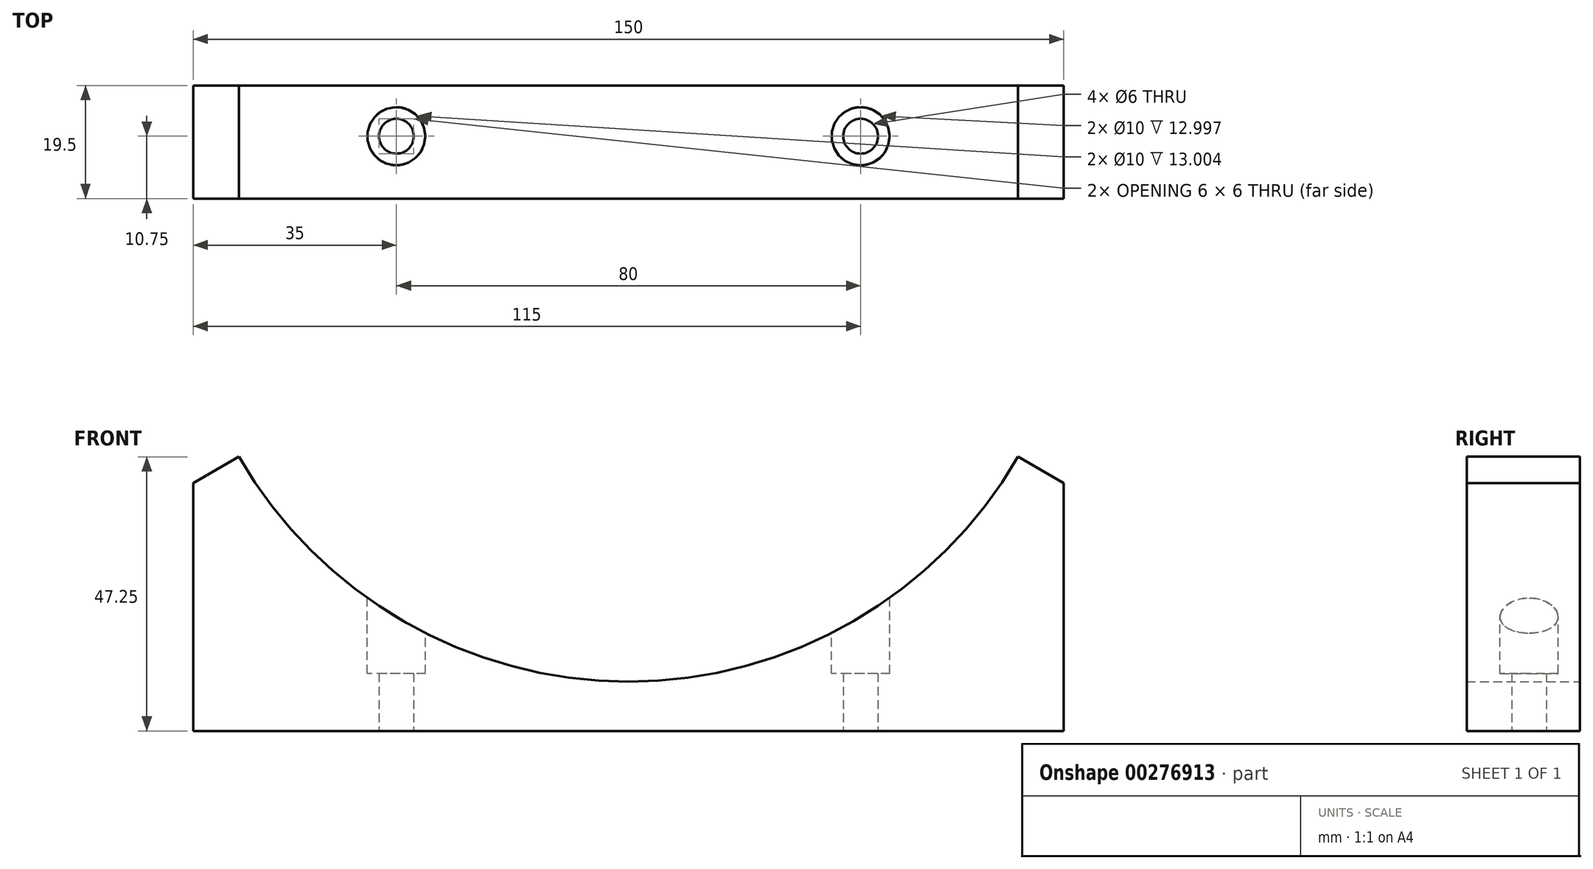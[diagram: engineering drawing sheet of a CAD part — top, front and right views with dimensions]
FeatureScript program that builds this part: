
annotation { "Feature Type Name" : "Feature", "Feature Type Description" : "" }
export const myFeature = defineFeature(function(context is Context, id is Id, definition is map)
    precondition{}
    {
        {
            var Q0;
            Q0=qCreatedBy(makeId("Front.planeOp"),FACE);
            var sketch = newSketch(context, id + "F0", { "sketchPlane" : qUnion([Q0])});
            skLineSegment(sketch, "E0.bottom", {"start": v(-75, -19.37) * mm, "end": v(75, -19.37) * mm});
            skLineSegment(sketch, "E0.left", {"start": v(-75, -19.37) * mm, "end": v(-75, 23.33) * mm});
            skLineSegment(sketch, "E0.right", {"start": v(75, -19.37) * mm, "end": v(75, 23.33) * mm});
            skLineSegment(sketch, "E1.trimOffspring", {"start": v(-67.12, 27.88) * mm, "end": v(-75, 23.33) * mm});
            skLineSegment(sketch, "E2.trimOffspring", {"start": v(67.12, 27.88) * mm, "end": v(75, 23.33) * mm});
            skLineSegment(sketch, "E3", {"start": v(0, 66.63) * mm, "end": v(0, -19.37) * mm, "construction": true});
            skPoint(sketch, "E3.endSnap0", {"position": v(0, -12) * mm});
            skLineSegment(sketch, "E4", {"start": v(0, 66.63) * mm, "end": v(75, 23.33) * mm, "construction": true});
            skArc(sketch, "E5", {"start": v(-67.12, 27.88) * mm, "mid": v(0, -10.87) * mm, "end": v(67.12, 27.88) * mm});
            skLineSegment(sketch, "E6", {"start": v(0, -19.37) * mm, "end": v(0, -10.87) * mm, "construction": true});
            skSolve(sketch);
        }
        {
            var Q0;
            Q0=qSketchRegion(id+"F0",true);
            extrude(context, id + "F1", {"entities" : qUnion([Q0]), "depth" : 19.5 * mm});
        }
        {
            var Q0;
            Q0=makeQuery(id+"F1.opExtrude","SWEPT_FACE",FACE,{"disambiguationData":[OSD([sQuery(id+"F0.wireOp",EDGE,"E0.bottom")])]});
            var sketch = newSketch(context, id + "F2", { "sketchPlane" : qUnion([Q0])});
            skCircle(sketch, "E7", {"center": v(40, 8.75) * mm, "radius": 3 * mm});
            skCircle(sketch, "E8", {"center": v(-40, 8.75) * mm, "radius": 3 * mm});
            skLineSegment(sketch, "E9", {"start": v(0, 0) * mm, "end": v(0, 19.5) * mm, "construction": true});
            skSolve(sketch);
        }
        {
            var Q0;
            Q0=makeQuery(id+"F2.imprint","IMPRINT",FACE,{"disambiguationData":[TD([[makeQuery(id+"F2.imprint","IMPRINT",EDGE,{"derivedFrom":sQuery(id+"F2.wireOp",EDGE,"E7")}),1.0]])]});
            var Q1;
            Q1=makeQuery(id+"F2.imprint","IMPRINT",FACE,{"disambiguationData":[TD([[makeQuery(id+"F2.imprint","IMPRINT",EDGE,{"derivedFrom":sQuery(id+"F2.wireOp",EDGE,"E8")}),1.0]])]});
            extrude(context, id + "F3", {"entities" : qUnion([Q0, Q1]), "operationType" : NewBodyOperationType.REMOVE, "endBound" : BoundingType.THROUGH_ALL, "oppositeDirection" : true, "depth" : 25 * mm});
        }
        {
            var Q0;
            Q0=qCreatedBy(makeId("Top.planeOp"),FACE);
            cPlane(context, id + "F4", {"entities" : qUnion([Q0]), "cplaneType" : CPlaneType.OFFSET, "offset" : 15 * mm, "width" : 150 * mm, "height" : 150 * mm});
        }
        {
            var Q0;
            Q0=qCreatedBy(id+"F4.planeOp",FACE);
            var sketch = newSketch(context, id + "F5", { "sketchPlane" : qUnion([Q0])});
            skCircle(sketch, "E10", {"center": v(-40, -8.75) * mm, "radius": 5 * mm});
            skCircle(sketch, "E11", {"center": v(40, -8.75) * mm, "radius": 5 * mm});
            skSolve(sketch);
        }
        {
            var Q0;
            Q0=makeQuery(id+"F5.imprint","IMPRINT",FACE,{"disambiguationData":[TD([[makeQuery(id+"F5.imprint","IMPRINT",EDGE,{"derivedFrom":sQuery(id+"F5.wireOp",EDGE,"E10")}),1.0]])]});
            var Q1;
            Q1=makeQuery(id+"F5.imprint","IMPRINT",FACE,{"disambiguationData":[TD([[makeQuery(id+"F5.imprint","IMPRINT",EDGE,{"derivedFrom":sQuery(id+"F5.wireOp",EDGE,"E11")}),1.0]])]});
            extrude(context, id + "F6", {"entities" : qUnion([Q0, Q1]), "operationType" : NewBodyOperationType.REMOVE, "oppositeDirection" : true, "depth" : 24.46 * mm});
        }
        {
            var Q0;
            Q0=qCreatedBy(makeId("Right.planeOp"),FACE);
            cPlane(context, id + "F7", {"entities" : qUnion([Q0]), "cplaneType" : CPlaneType.OFFSET, "offset" : 36 * mm, "width" : 150 * mm, "height" : 150 * mm});
        }
        {
            var Q0;
            Q0=makeQuery(id+"F1.opExtrude","SWEPT_BODY",BODY,{"disambiguationData":[OSD([sQuery(id+"F0.wireOp",EDGE,"E0.bottom"),sQuery(id+"F0.wireOp",EDGE,"E0.left"),sQuery(id+"F0.wireOp",EDGE,"E0.right"),sQuery(id+"F0.wireOp",EDGE,"E1.trimOffspring"),sQuery(id+"F0.wireOp",EDGE,"E2.trimOffspring"),sQuery(id+"F0.wireOp",EDGE,"E5")])]});
            transform(context, id + "F8", {"entities" : qUnion([Q0]), "transformType" : TransformType.TRANSLATION_3D, "dx" : 0 * mm, "dy" : 0 * mm, "dz" : 0 * mm, "makeCopy" : true});
        }
    });
